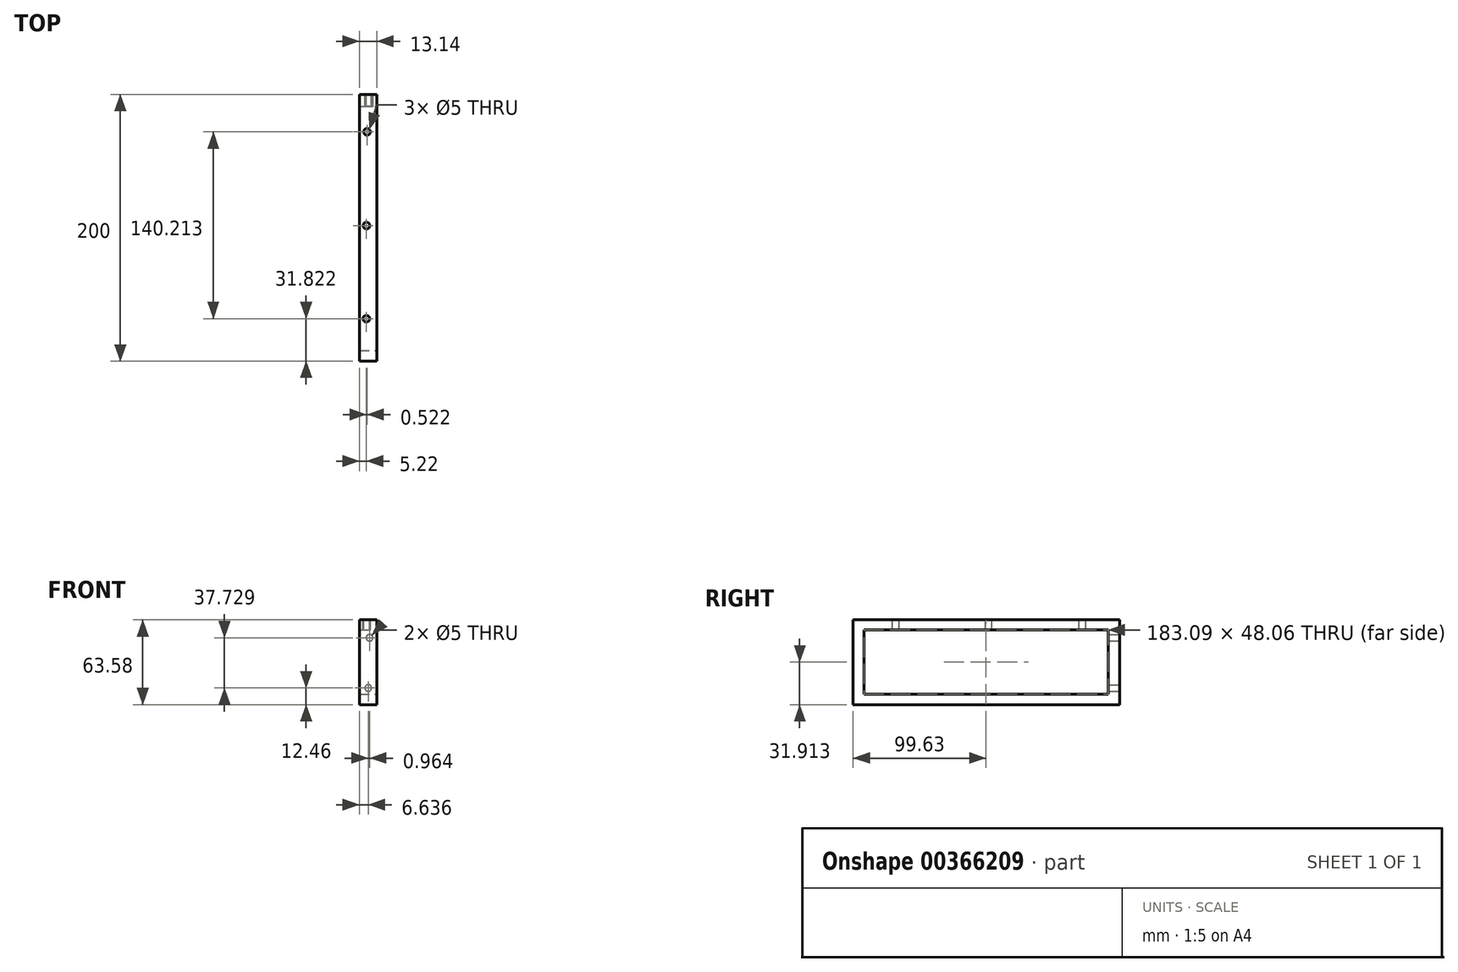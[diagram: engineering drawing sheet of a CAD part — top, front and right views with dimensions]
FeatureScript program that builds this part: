
annotation { "Feature Type Name" : "Feature", "Feature Type Description" : "" }
export const myFeature = defineFeature(function(context is Context, id is Id, definition is map)
    precondition{}
    {
        {
            var Q0;
            Q0=qCreatedBy(makeId("Front.planeOp"),FACE);
            var sketch = newSketch(context, id + "F0", { "sketchPlane" : qUnion([Q0])});
            skLineSegment(sketch, "E0.bottom", {"start": v(-68.3, 25.52) * mm, "end": v(-55.16, 25.52) * mm});
            skLineSegment(sketch, "E0.top", {"start": v(-68.3, -38.06) * mm, "end": v(-55.16, -38.06) * mm});
            skLineSegment(sketch, "E0.left", {"start": v(-68.3, 25.52) * mm, "end": v(-68.3, -38.06) * mm});
            skLineSegment(sketch, "E0.right", {"start": v(-55.16, 25.52) * mm, "end": v(-55.16, -38.06) * mm});
            skSolve(sketch);
        }
        {
            var Q0;
            Q0=makeQuery(id+"F0.imprint","IMPRINT",FACE,{"disambiguationData":[TD([[makeQuery(id+"F0.imprint","IMPRINT",EDGE,{"derivedFrom":sQuery(id+"F0.wireOp",EDGE,"E0.bottom")}),-1.0]])]});
            extrude(context, id + "F1", {"entities" : qUnion([Q0]), "depth" : 200 * mm});
        }
        {
            var Q0;
            Q0=makeQuery(id+"F1.opExtrude","SWEPT_FACE",FACE,{"disambiguationData":[OSD([sQuery(id+"F0.wireOp",EDGE,"E0.bottom")])]});
            var sketch = newSketch(context, id + "F2", { "sketchPlane" : qUnion([Q0])});
            skPoint(sketch, "E1", {"position": v(-63.08, -168.18) * mm});
            skPoint(sketch, "E2", {"position": v(-62.98, -98.36) * mm});
            skPoint(sketch, "E3", {"position": v(-62.56, -27.97) * mm});
            skSolve(sketch);
        }
        {
            var Q0;
            Q0=sQuery(id+"F2.wireOp",VERTEX,"E1");
            var Q1;
            Q1=sQuery(id+"F2.wireOp",VERTEX,"E2");
            var Q2;
            Q2=sQuery(id+"F2.wireOp",VERTEX,"E3");
            var Q3;
            Q3=makeQuery(id+"F1.opExtrude","SWEPT_BODY",BODY,{"disambiguationData":[OSD([sQuery(id+"F0.wireOp",EDGE,"E0.bottom"),sQuery(id+"F0.wireOp",EDGE,"E0.top"),sQuery(id+"F0.wireOp",EDGE,"E0.left"),sQuery(id+"F0.wireOp",EDGE,"E0.right")])]});
            hole(context, id + "F3", {"style" : HoleStyle.SIMPLE, "endStyle" : HoleEndStyle.BLIND, "holeDiameter" : 5 * mm, "holeDepth" : 12 * mm, "isTappedThrough" : true, "tappedDepth" : 12 * mm, "tapClearance" : 3, "locations" : qUnion([Q0, Q1, Q2]), "scope" : qUnion([Q3])});
        }
        {
            var Q0;
            Q0=makeQuery(id+"F0.imprint","IMPRINT",FACE,{"disambiguationData":[TD([[makeQuery(id+"F0.imprint","IMPRINT",EDGE,{"derivedFrom":sQuery(id+"F0.wireOp",EDGE,"E0.bottom")}),-1.0]])]});
            var sketch = newSketch(context, id + "F4", { "sketchPlane" : qUnion([Q0])});
            skPoint(sketch, "E4", {"position": v(-60.7, 12.13) * mm});
            skPoint(sketch, "E5", {"position": v(-61.66, -25.6) * mm});
            skSolve(sketch);
        }
        {
            var Q0;
            Q0=sQuery(id+"F4.wireOp",VERTEX,"E4");
            var Q1;
            Q1=sQuery(id+"F4.wireOp",VERTEX,"E5");
            var Q2;
            Q2=makeQuery(id+"F1.opExtrude","SWEPT_BODY",BODY,{"disambiguationData":[OSD([sQuery(id+"F0.wireOp",EDGE,"E0.bottom"),sQuery(id+"F0.wireOp",EDGE,"E0.top"),sQuery(id+"F0.wireOp",EDGE,"E0.left"),sQuery(id+"F0.wireOp",EDGE,"E0.right")])]});
            hole(context, id + "F5", {"style" : HoleStyle.SIMPLE, "endStyle" : HoleEndStyle.BLIND, "oppositeDirection" : true, "holeDiameter" : 5 * mm, "holeDepth" : 12 * mm, "isTappedThrough" : true, "tappedDepth" : 12 * mm, "tapClearance" : 3, "locations" : qUnion([Q0, Q1]), "scope" : qUnion([Q2])});
        }
        {
            var Q0;
            Q0=makeQuery(id+"F1.opExtrude","SWEPT_FACE",FACE,{"disambiguationData":[OSD([sQuery(id+"F0.wireOp",EDGE,"E0.right")])]});
            var sketch = newSketch(context, id + "F6", { "sketchPlane" : qUnion([Q0])});
            skLineSegment(sketch, "E6.bottom", {"start": v(-191.92, 17.89) * mm, "end": v(-8.82, 17.89) * mm});
            skLineSegment(sketch, "E6.top", {"start": v(-191.92, -30.18) * mm, "end": v(-8.82, -30.18) * mm});
            skLineSegment(sketch, "E6.left", {"start": v(-191.92, 17.89) * mm, "end": v(-191.92, -30.18) * mm});
            skLineSegment(sketch, "E6.right", {"start": v(-8.82, 17.89) * mm, "end": v(-8.82, -30.18) * mm});
            skSolve(sketch);
        }
        {
            var Q0;
            Q0 = qSketchRegion(id + "F6", true);
            extrude(context, id + "F7", {"entities" : qUnion([Q0]), "operationType" : NewBodyOperationType.REMOVE, "oppositeDirection" : true, "depth" : 25 * mm});
        }
    });
